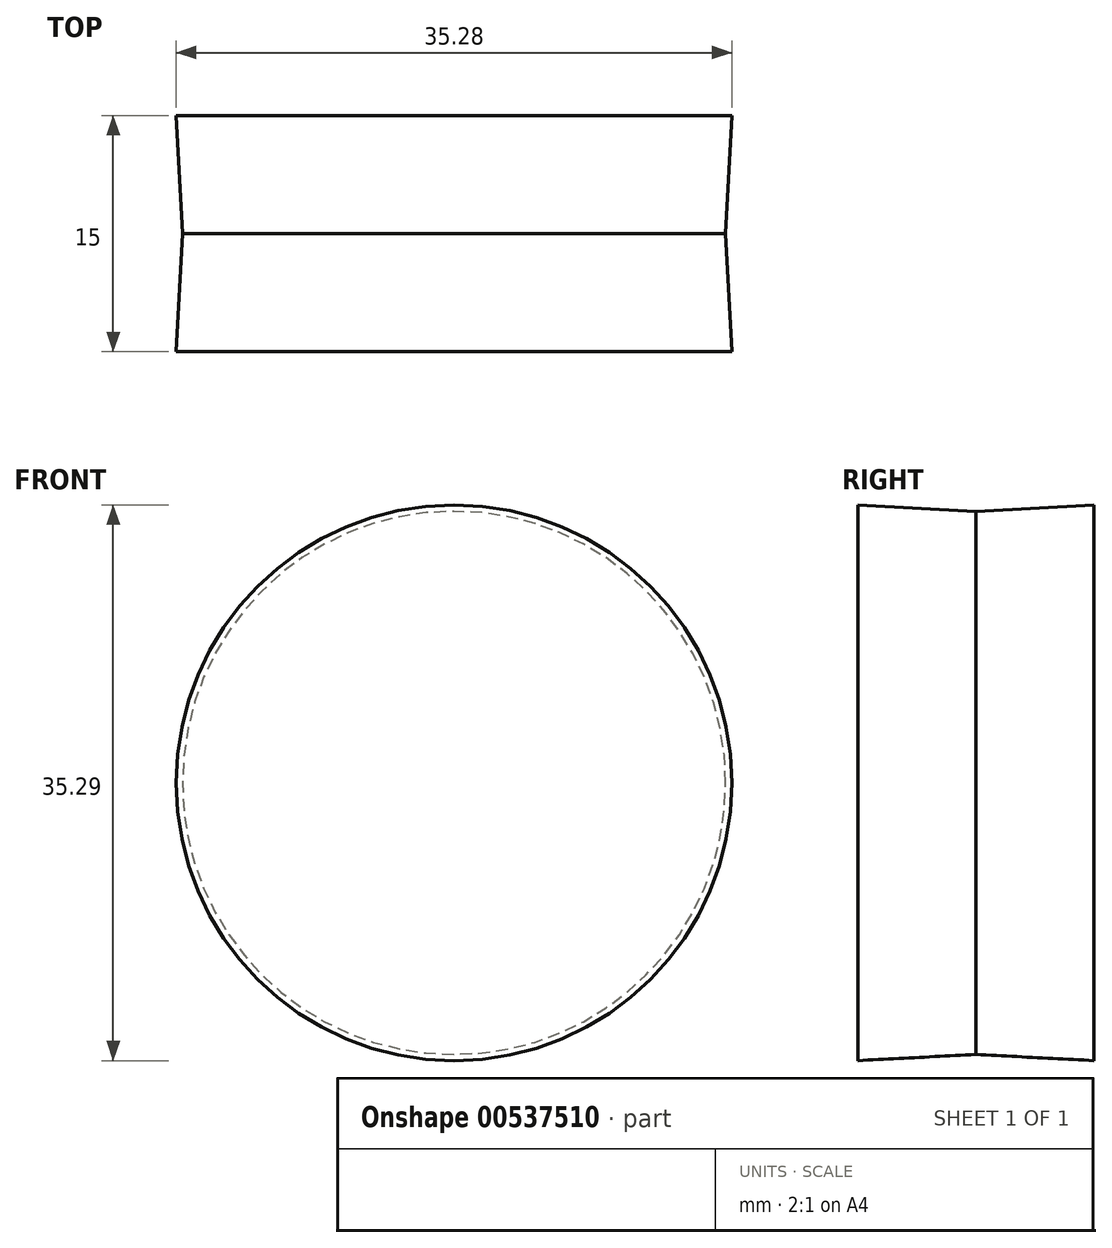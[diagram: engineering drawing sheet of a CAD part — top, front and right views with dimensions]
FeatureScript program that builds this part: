
annotation { "Feature Type Name" : "Feature", "Feature Type Description" : "" }
export const myFeature = defineFeature(function(context is Context, id is Id, definition is map)
    precondition{}
    {
        {
            var Q0;
            Q0=qCreatedBy(makeId("Front.planeOp"),FACE);
            var sketch = newSketch(context, id + "F0", { "sketchPlane" : qUnion([Q0])});
            skCircle(sketch, "E0", {"center": v(0.19, -0.01) * mm, "radius": 17.25 * mm});
            skSolve(sketch);
        }
        {
            var Q0;
            Q0=qCreatedBy(makeId("Right.planeOp"),FACE);
            var sketch = newSketch(context, id + "F1", { "sketchPlane" : qUnion([Q0])});
            skLineSegment(sketch, "E1.bottom", {"start": v(-7.5, 17.25) * mm, "end": v(7.5, 17.25) * mm});
            skLineSegment(sketch, "E1.top", {"start": v(-7.5, -17.25) * mm, "end": v(7.5, -17.25) * mm});
            skLineSegment(sketch, "E1.left", {"start": v(-7.5, 17.25) * mm, "end": v(-7.5, -17.25) * mm});
            skLineSegment(sketch, "E1.right", {"start": v(7.5, 17.25) * mm, "end": v(7.5, -17.25) * mm});
            skPoint(sketch, "E1.middle", {"position": v(0, 0) * mm});
            skSolve(sketch);
        }
        {
            var Q0;
            Q0=makeQuery(id+"F0.imprint","IMPRINT",FACE,{"disambiguationData":[TD([[makeQuery(id+"F0.imprint","IMPRINT",EDGE,{"derivedFrom":sQuery(id+"F0.wireOp",EDGE,"E0")}),1.0]])]});
            extrude(context, id + "F2", {"entities" : qUnion([Q0]), "endBound" : BoundingType.SYMMETRIC, "depth" : 15 * mm, "offsetDistance" : 25 * mm, "hasDraft" : true, "draftAngle" : 3 * degree});
        }
    });
